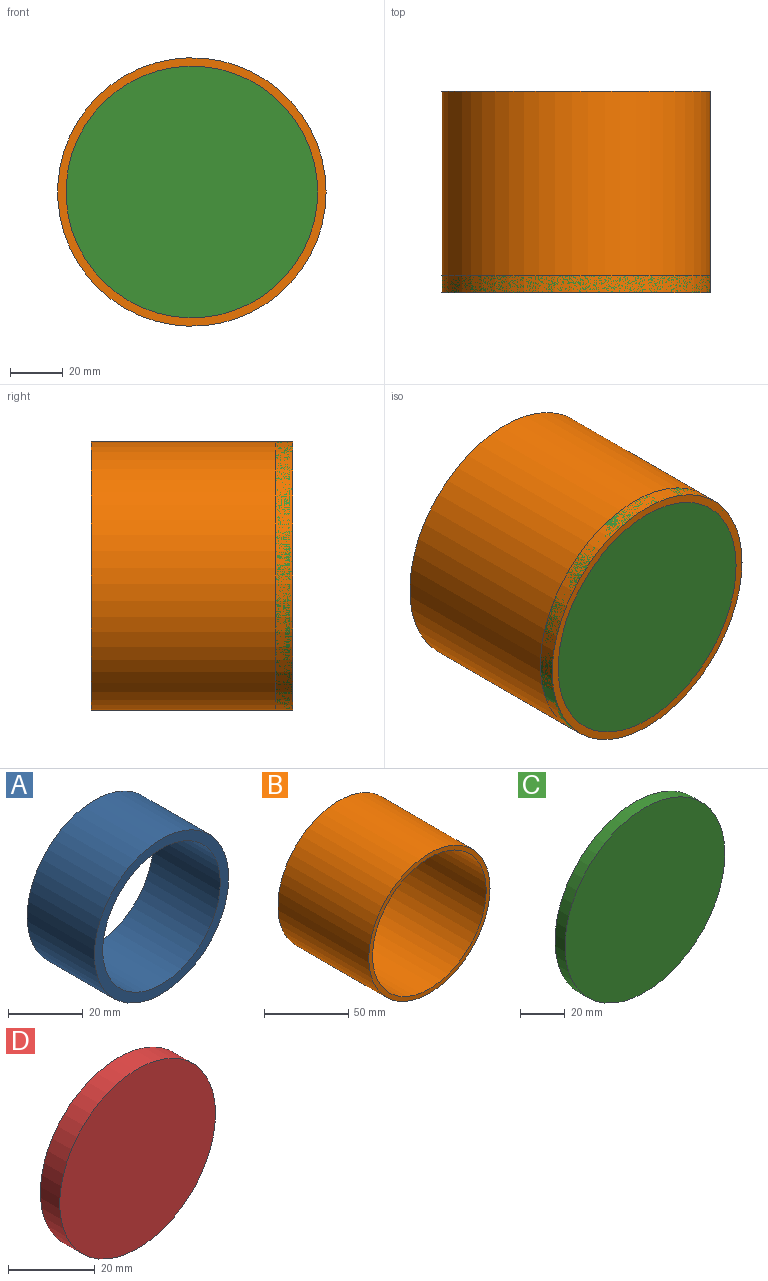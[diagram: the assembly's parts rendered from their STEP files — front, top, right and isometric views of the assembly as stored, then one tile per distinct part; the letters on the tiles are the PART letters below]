
ASSEMBLY  parts=4 mates=3
PART A: 4 faces, bbox 50.8x25.4x50.8 mm
  f0: cylinder r=22.23mm len=44.45mm, axis (0,1,0), area 3547mm2, adj f2,f3
  f1: cylinder r=25.4mm len=50.8mm, axis (0,1,0), area 4053.7mm2, adj f2,f3
  f2: plane 50.8x50.8mm, normal (0,-1,0), area 475mm2, adj f0,f1
  f3: plane 50.8x50.8mm, normal (0,1,0), area 475mm2, adj f0,f1
PART B: 4 faces, bbox 101.6x76.2x101.6 mm
  f0: cylinder r=47.62mm len=95.25mm, axis (0,1,0), area 22801.8mm2, adj f2,f3
  f1: cylinder r=50.8mm len=101.6mm, axis (0,1,0), area 24322mm2, adj f2,f3
  f2: plane 101.6x101.6mm, normal (0,-1,0), area 981.7mm2, adj f0,f1
  f3: plane 101.6x101.6mm, normal (0,1,0), area 981.7mm2, adj f0,f1
PART C: 3 faces, bbox 101.6x6.4x101.6 mm
  f0: cylinder r=50.8mm len=101.6mm, axis (0,-1,0), area 2026.8mm2, adj f1,f2
  f1: plane 101.6x101.6mm, normal (0,1,0), area 8107.3mm2, adj f0
  f2: plane 101.6x101.6mm, normal (0,-1,0), area 8107.3mm2, adj f0
PART D: 3 faces, bbox 50.8x6.4x50.8 mm
  f0: cylinder r=25.4mm len=50.8mm, axis (0,-1,0), area 1013.4mm2, adj f1,f2
  f1: plane 50.8x50.8mm, normal (0,1,0), area 2026.8mm2, adj f0
  f2: plane 50.8x50.8mm, normal (0,-1,0), area 2026.8mm2, adj f0
PLACE A t=(-215.62,115.41,-137.17)mm
PLACE B t=(-122.15,163.96,-137.17)mm
PLACE C t=(-122.15,87.76,-137.17)mm
PLACE D t=(-215.62,90.01,-137.17)mm
MATE slider D.f0 <-> C.f0  axis (0,1,0) through (-170.45,96.36,-137.17)mm
MATE fastened D.f0 <-> A.f0  axis (0,-1,0) through (-170.45,90.01,-137.17)mm
MATE fastened B.f0 <-> C.f0  axis (0,-1,0) through (-170.45,87.76,-137.17)mm
